# Revit family: xLIFE-PRO-WP-IPREM_Wall-Hosted_R16
name_source: partatom
category: Lighting Fixtures
revit_build: Autodesk Revit 2016 (Build: 20150220_1215(x64)
units: mm (PartAtom-declared; Revit-internal decimal feet)

## family parameters
Always vertical = Yes
Cut with Voids When Loaded = No
Host = Wall
Light Source = Yes
OmniClass Number = 23.80.70.00
OmniClass Title = Lighting
Part Type = Normal
Room Calculation Point = No
Round Connector Dimension = Use Diameter
Shared = No

## types (2) — shared parameters
AS2293 Classification = C0=D40 C90=D50
Color Filter = 16777215
Construction = Polycarbonate
Dimensions LED Enclosure (L x W x H) = 122mm x 120mm x x75mm (Lamp head enclosure)
Dimensions Main Enclosure (L x W x H) = 380mm x 190mm x 130mm (Control pack)
Dimming Lamp Color Temperature Shift = <None>
Emit Shape Visible in Rendering = No
Emit from Circle Diameter = 610 mm
IK Rating = IK08
IP Rating = IP66/67
Manufacturer = Clevertronics
Mounting = Surface mount
Operating Mode = Non-maintained
Operating Temperature = 0˚ to 40˚C (Ambient) (Control Gear)
-40˚ to 40˚C (Lamp Head Assembly)
Operating Voltage = 240V AC; 50Hz
Photometric Web File = 669-2_LLIFE-PRO-WP_pin_cutted_550mA_26072017-02_R4p.ies
Power Consumption = 0.4 Watts (Standby), 4.7 Watts (Max)
Testing System = Clevertest Plus Enabled (Not activated by default)
Tilt Angle = 90.00°
Total Lumen Output = 307

## per-type parameters (varying)
| type | Battery | Battery type | Charger Method | Lamp | MIC Number | Product Description | Replacement Battery | Replacement Driver | Replacement Lamp |
| CLIFE-PRO-WP-IPREM | 3.2V 6400mAh | Lithium Iron Phosphate | Intelligent current limited constant voltage | Dual LED (Lifetime warranty on the lamp head and loom assembly) | AUT02320050001 | LP Premium LifeLight Pro, High Performance, Surface Mounted Emergency Light | BATT:LP 3.2V 6400mAh.200mm lead.Brkt. | LifelightPro,Control Only,Batten,LP, NP | 1100828 Lifelight Pro Head Assembly, Round, Gen 2 |
| LLIFE-PRO-WP-IPREM | 3.3V 5000mAh | Lithium Nanophosphate | Intelligent Current Limited Constant Voltage | 2 x 3W LED (Lifetime warranty on the Lamp head and loom Assembly) | AUT01320100001 | L10 Optimum Lifelight PRO, High Performance | 1530230 BATTERY:L10 3.3V 5AH. 200mm lead.Brkt | LLIFE-PRO-CKIT  Lifelight Pro, Control Only, LP/L10 | 1100696 Lifelight Pro, WP Head, Gen 2 |

note: column(s) folded — value = type name in every type: Model

## geometry (parser evidence)
native form markers: Sweep x3
no freeform markers — native parametric forms only
